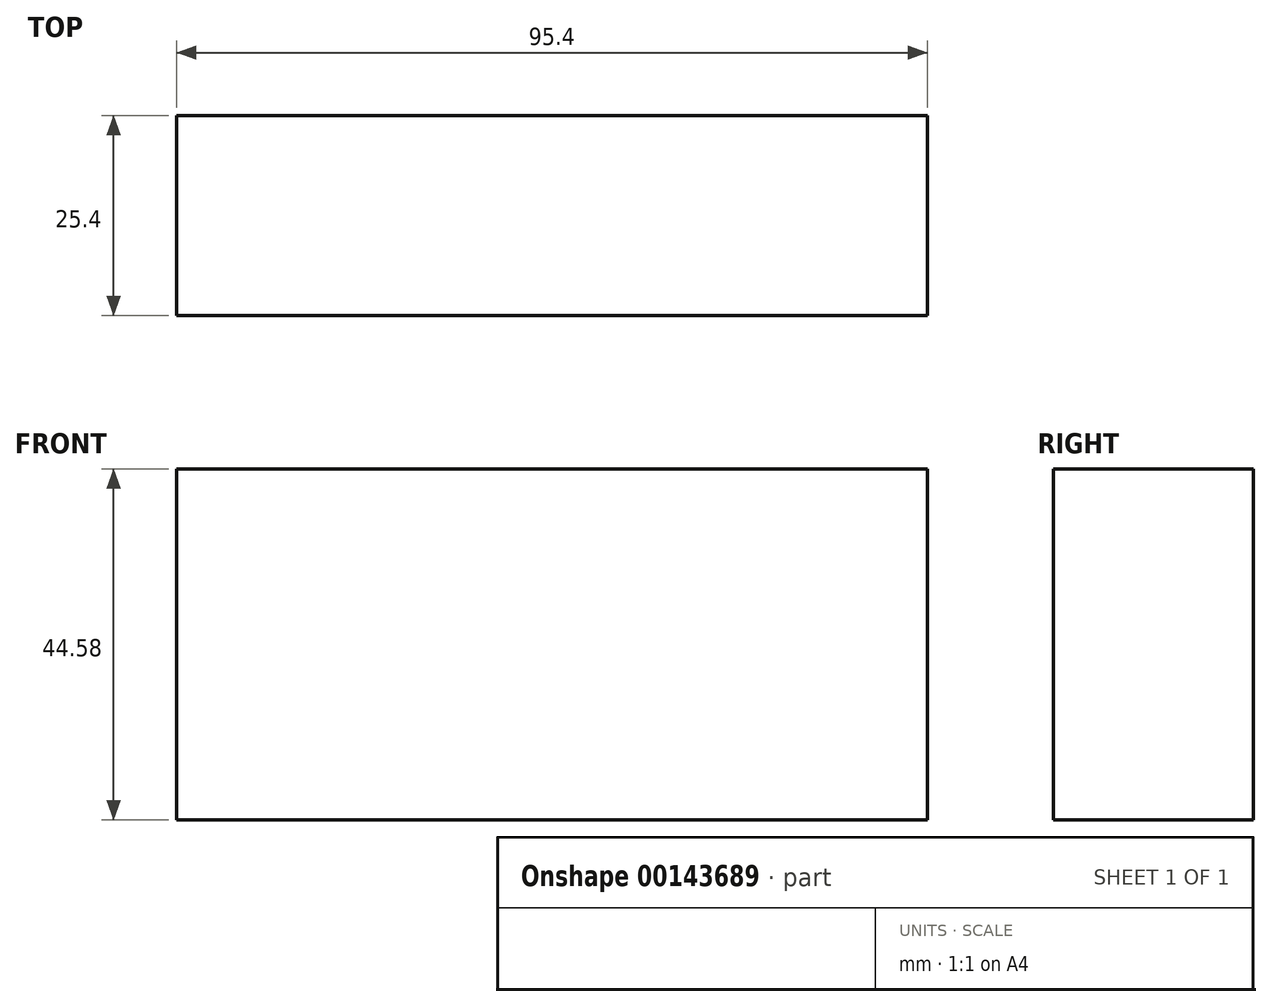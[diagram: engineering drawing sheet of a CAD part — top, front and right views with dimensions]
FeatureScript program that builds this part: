
annotation { "Feature Type Name" : "Feature", "Feature Type Description" : "" }
export const myFeature = defineFeature(function(context is Context, id is Id, definition is map)
    precondition{}
    {
        {
            var Q0;
            Q0=qCreatedBy(makeId("Front.planeOp"),FACE);
            var sketch = newSketch(context, id + "F0", { "sketchPlane" : qUnion([Q0])});
            skLineSegment(sketch, "E0.bottom", {"start": v(47.7, 22.29) * mm, "end": v(-47.7, 22.29) * mm});
            skLineSegment(sketch, "E0.top", {"start": v(47.7, -22.29) * mm, "end": v(-47.7, -22.29) * mm});
            skLineSegment(sketch, "E0.left", {"start": v(47.7, 22.29) * mm, "end": v(47.7, -22.29) * mm});
            skLineSegment(sketch, "E0.right", {"start": v(-47.7, 22.29) * mm, "end": v(-47.7, -22.29) * mm});
            skPoint(sketch, "E0.middle", {"position": v(0, 0) * mm});
            skSolve(sketch);
        }
        {
            var Q0;
            Q0 = qSketchRegion(id + "F0", true);
            extrude(context, id + "F1", {"entities" : qUnion([Q0]), "endBound" : BoundingType.SYMMETRIC, "depth" : 25.4 * mm});
        }
    });
